# Revit family: 201_ILO-Z-_-_
name_source: partatom
category: Air Terminals
units: mm (PartAtom-declared; Revit-internal decimal feet)

## family parameters
Always vertical = Yes
Cut with Voids When Loaded = No
Part Type = Normal
Room Calculation Point = Yes
Round Connector Dimension = Use Diameter
Shared = No
Work Plane-Based = No

## types (8) — shared parameters
CAT0 = Yes
CL_Location_5000 = 5000 mm  [stored 16.4042 ft]
Description = Swirl diffuser for ceiling. "Tegular" type
H1 = 2 mm  [stored 0.00656168 ft]
L_ARR = 400 mm  [stored 1.31234 ft]
Manufacturer = Climecon
QmdConnectorList = 201;D
R = 10 mm  [stored 0.0328084 ft]
URL = www.climecon.fi
W_ARR = 400 mm  [stored 1.31234 ft]
XRefLineVPlnId = 7453
YRefLineVPlnId = 7456
Z1 = Yes
Z2 = 8 mm  [stored 0.0262467 ft]
Z2__ve = -8 mm  [stored -0.0262467 ft]
magiPartTypeId = 201
magiProductFamilyId = ILO-Z-*-*
zero-valued in all types: CLBTZ, H_ARR, MC_Default_elevation

## per-type parameters (varying)
| type | AA | AX | BB | D | HX |
| ILO-Z-125-400 | 198 mm | 187 mm | 172 mm | 125 mm | 51 mm  [stored 0.167323 ft] |
| ILO-Z-315-600 | 298 mm | 287 mm | 272 mm | 315 mm | 71 mm  [stored 0.23294 ft] |
| ILO-Z-250-600 | 298 mm | 287 mm | 272 mm | 250 mm | 71 mm  [stored 0.23294 ft] |
| ILO-Z-200-600 | 298 mm | 287 mm | 272 mm | 200 mm | 71 mm  [stored 0.23294 ft] |
| ILO-Z-200-400 | 198 mm | 187 mm | 172 mm | 200 mm | 51 mm  [stored 0.167323 ft] |
| ILO-Z-160-600 | 298 mm | 287 mm | 272 mm | 160 mm | 51 mm  [stored 0.167323 ft] |
| ILO-Z-160-400 | 198 mm | 187 mm | 172 mm | 160 mm | 51 mm  [stored 0.167323 ft] |
| ILO-Z-125-600 | 298 mm | 287 mm | 272 mm | 125 mm | 51 mm  [stored 0.167323 ft] |

note: column(s) folded — value = type name in every type: magiProductCode, magiProductId

note: [stored X ft] marks values corroborated as IEEE doubles in the binary element streams (Revit-internal decimal feet)

## geometry (parser evidence)
native form markers: Sweep x1
no freeform markers — native parametric forms only
